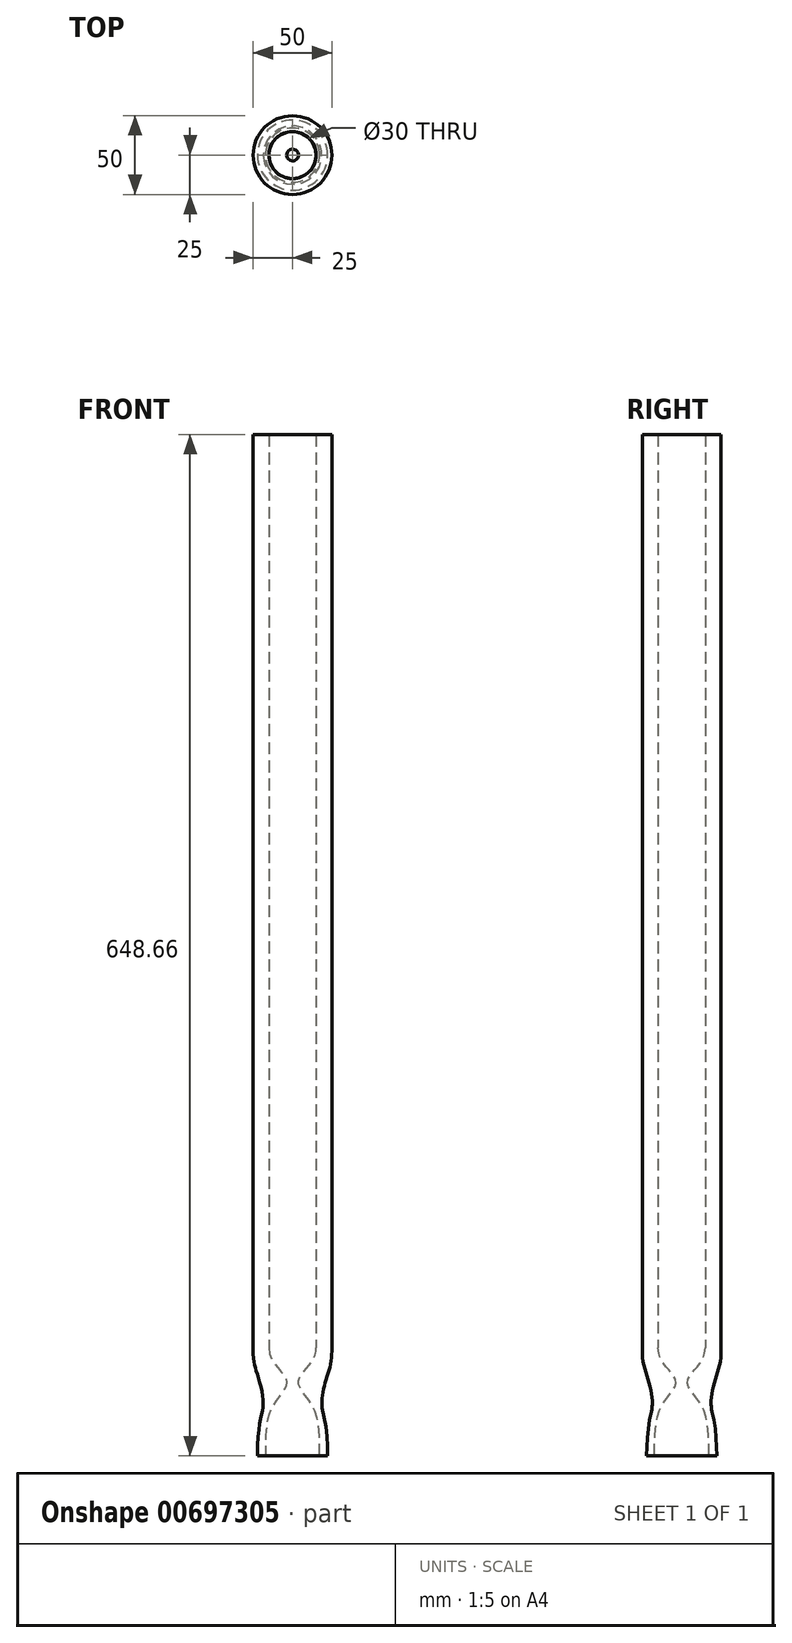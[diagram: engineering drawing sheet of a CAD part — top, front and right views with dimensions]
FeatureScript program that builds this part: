
annotation { "Feature Type Name" : "Feature", "Feature Type Description" : "" }
export const myFeature = defineFeature(function(context is Context, id is Id, definition is map)
    precondition{}
    {
        {
            var Q0;
            Q0=qCreatedBy(makeId("Front.planeOp"),FACE);
            var sketch = newSketch(context, id + "F0", { "sketchPlane" : qUnion([Q0])});
            skLineSegment(sketch, "E0", {"start": v(-15, -104.2) * mm, "end": v(-15, 475.8) * mm});
            skLineSegment(sketch, "E1", {"start": v(0, -172.86) * mm, "end": v(0, 525.99) * mm, "construction": true});
            skLineSegment(sketch, "E2", {"start": v(-44.53, -172.86) * mm, "end": v(0, -172.86) * mm, "construction": true});
            skFitSpline(sketch, "E3", {"points": [v(-15, -104.2) * mm, v(-3.82, -125.18) * mm, v(-12.58, -141.04) * mm, v(-17.26, -172.86) * mm], "startDerivative": vector(0, -93.02) * mm, "endDerivative": vector(0, -102.86) * mm});
            skLineSegment(sketch, "E4", {"start": v(-3.74, -149.01) * mm, "end": v(-3.74, -119.98) * mm, "construction": true});
            skFitSpline(sketch, "E5", {"points": [v(-25, -104.48) * mm, v(-22.8, -119.63) * mm, v(-18.62, -138.6) * mm, v(-22.26, -172.86) * mm], "startDerivative": vector(0, -91.9) * mm, "endDerivative": vector(0, -165.94) * mm});
            skLineSegment(sketch, "E6", {"start": v(-22.26, -172.86) * mm, "end": v(-17.26, -172.86) * mm});
            skLineSegment(sketch, "E7", {"start": v(-25, -104.2) * mm, "end": v(-25, 475.8) * mm});
            skLineSegment(sketch, "E8", {"start": v(-15, 475.8) * mm, "end": v(-25, 475.8) * mm});
            skLineSegment(sketch, "E9", {"start": v(-25, -104.2) * mm, "end": v(-25, -104.48) * mm});
            skSolve(sketch);
        }
        {
            var Q0;
            Q0 = qSketchRegion(id + "F0", true);
            var Q1;
            Q1=sQuery(id+"F0.wireOp",EDGE,"E1");
            revolve(context, id + "F1", {"surfaceOperationType" : NewSurfaceOperationType.NEW, "entities" : qUnion([Q0]), "axis" : qUnion([Q1]), "revolveType" : RevolveType.FULL});
        }
    });
